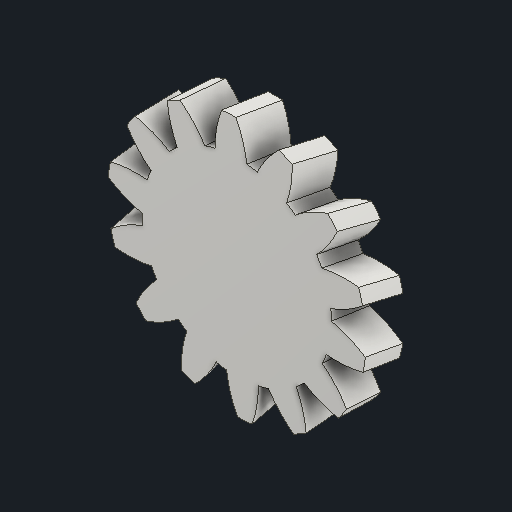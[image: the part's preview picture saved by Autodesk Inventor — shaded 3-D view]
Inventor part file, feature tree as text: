
AUTODESK INVENTOR PART (.ipt)
format: ipt  version: 2024.2 (Build 282272000, 272)  size: 327,680 bytes
history: native  units: mm (DEFAULTED — no unit token found)
features: plane x3, other x3, extrude x1, sketch x1
ambient origin geometry x8: Origin, YZ Plane, XZ Plane, XY Plane, X Axis, Y Axis, Z Axis, Center Point
bodies: Solid1 (feature_tree)
feature tree (8):
  extrude  "Extrusion1"  Depth=6.35mm TaperAngle=0.0deg
  plane  "Work Plane1"
  plane  "Work Plane2"
  plane  "Work Plane3"
  other  "Spur Gear"
  sketch  "Sketch1"  dims[d0=42.577228mm d1=6.35mm d2=0.0mm d3=36.10857mm d4=76.2mm d5=0.0mm d6=0.0mm d7=2.243995mm d9=0.0mm d14=0.0mm d15=35.513307mm d16=0.0mm d17=0.0mm d18=0.0mm d19=35.513307mm]
  other  "Srf1"
  other  "Pitch Diameter"
